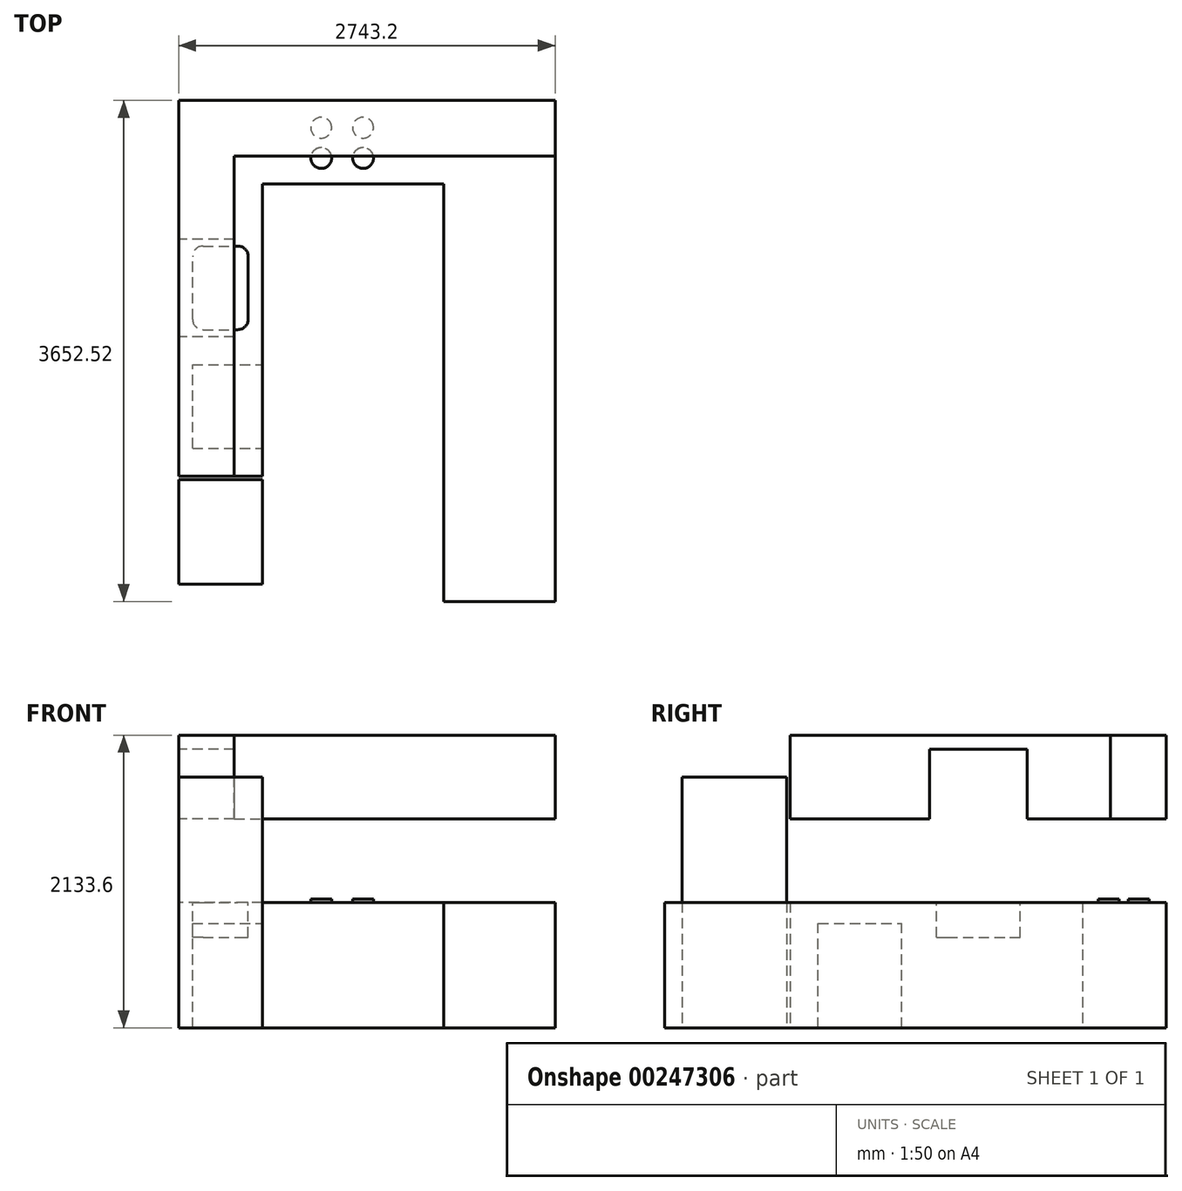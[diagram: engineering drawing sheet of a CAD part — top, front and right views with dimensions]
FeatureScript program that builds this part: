
annotation { "Feature Type Name" : "Feature", "Feature Type Description" : "" }
export const myFeature = defineFeature(function(context is Context, id is Id, definition is map)
    precondition{}
    {
        {
            var Q0;
            Q0=qCreatedBy(makeId("Top.planeOp"),FACE);
            var sketch = newSketch(context, id + "F0", { "sketchPlane" : qUnion([Q0])});
            skLineSegment(sketch, "E0.bottom", {"start": v(1371.6, -1826.26) * mm, "end": v(558.8, -1826.26) * mm});
            skLineSegment(sketch, "E0.top", {"start": v(1371.6, 1826.26) * mm, "end": v(-1371.6, 1826.26) * mm});
            skLineSegment(sketch, "E0.left", {"start": v(1371.6, -1826.26) * mm, "end": v(1371.6, 1826.26) * mm});
            skLineSegment(sketch, "E0.right", {"start": v(-1371.6, -911.86) * mm, "end": v(-1371.6, 1826.26) * mm});
            skPoint(sketch, "E0.middle", {"position": v(0, 0) * mm});
            skLineSegment(sketch, "E1.0", {"start": v(-762, -911.86) * mm, "end": v(-762, 1216.66) * mm});
            skLineSegment(sketch, "E2.0", {"start": v(558.8, 1216.66) * mm, "end": v(-762, 1216.66) * mm});
            skLineSegment(sketch, "E3.0", {"start": v(558.8, -1826.26) * mm, "end": v(558.8, 1216.66) * mm});
            skLineSegment(sketch, "E4.0", {"start": v(-762, -911.86) * mm, "end": v(-1371.6, -911.86) * mm});
            skPoint(sketch, "E5.orphan", {"position": v(-1371.6, -1826.26) * mm});
            skSolve(sketch);
        }
        {
            var Q0;
            Q0 = qSketchRegion(id + "F0", true);
            extrude(context, id + "F1", {"entities" : qUnion([Q0]), "depth" : 914.4 * mm});
        }
        {
            var Q0;
            Q0=qCreatedBy(makeId("Top.planeOp"),FACE);
            var sketch = newSketch(context, id + "F2", { "sketchPlane" : qUnion([Q0])});
            skLineSegment(sketch, "E6.top", {"start": v(-1371.6, -1699.26) * mm, "end": v(-762, -1699.26) * mm});
            skLineSegment(sketch, "E6.left", {"start": v(-1371.6, -937.26) * mm, "end": v(-1371.6, -1699.26) * mm});
            skLineSegment(sketch, "E6.right", {"start": v(-762, -937.26) * mm, "end": v(-762, -1699.26) * mm});
            skLineSegment(sketch, "E7", {"start": v(-1371.6, -937.26) * mm, "end": v(-762, -937.26) * mm});
            skSolve(sketch);
        }
        {
            var Q0;
            Q0 = qSketchRegion(id + "F2", true);
            extrude(context, id + "F3", {"entities" : qUnion([Q0]), "operationType" : NewBodyOperationType.ADD, "depth" : 1828.8 * mm});
        }
        {
            var Q0;
            Q0=makeQuery(id+"F1.opExtrude","SWEPT_FACE",FACE,{"disambiguationData":[OSD([sQuery(id+"F0.wireOp",EDGE,"E1.0")])]});
            var sketch = newSketch(context, id + "F4", { "sketchPlane" : qUnion([Q0])});
            skLineSegment(sketch, "E8.bottom", {"start": v(-708.66, 0) * mm, "end": v(-99.06, 0) * mm});
            skLineSegment(sketch, "E8.top", {"start": v(-708.66, 762) * mm, "end": v(-99.06, 762) * mm});
            skLineSegment(sketch, "E8.left", {"start": v(-708.66, 0) * mm, "end": v(-708.66, 762) * mm});
            skLineSegment(sketch, "E8.right", {"start": v(-99.06, 0) * mm, "end": v(-99.06, 762) * mm});
            skSolve(sketch);
        }
        {
            var Q0;
            Q0 = qSketchRegion(id + "F4", true);
            extrude(context, id + "F5", {"entities" : qUnion([Q0]), "operationType" : NewBodyOperationType.REMOVE, "oppositeDirection" : true, "depth" : 508 * mm});
        }
        {
            var Q0;
            Q0=makeQuery(id+"F1.opExtrude","CAP_FACE",FACE,{"disambiguationData":[OSD([sQuery(id+"F0.wireOp",EDGE,"E0.bottom"),sQuery(id+"F0.wireOp",EDGE,"E0.top"),sQuery(id+"F0.wireOp",EDGE,"E0.left"),sQuery(id+"F0.wireOp",EDGE,"E0.right"),sQuery(id+"F0.wireOp",EDGE,"E1.0"),sQuery(id+"F0.wireOp",EDGE,"E2.0"),sQuery(id+"F0.wireOp",EDGE,"E3.0"),sQuery(id+"F0.wireOp",EDGE,"E4.0")])],"isStart":false});
            var sketch = newSketch(context, id + "F6", { "sketchPlane" : qUnion([Q0])});
            skLineSegment(sketch, "E9.bottom", {"start": v(-1193.8, 154.94) * mm, "end": v(-939.8, 154.94) * mm});
            skLineSegment(sketch, "E9.top", {"start": v(-1193.8, 764.54) * mm, "end": v(-939.8, 764.54) * mm});
            skLineSegment(sketch, "E9.left", {"start": v(-1270, 231.14) * mm, "end": v(-1270, 688.34) * mm});
            skLineSegment(sketch, "E9.right", {"start": v(-863.6, 231.14) * mm, "end": v(-863.6, 688.34) * mm});
            skPoint(sketch, "E10.visualSharp", {"position": v(-1270, 154.94) * mm});
            skArc(sketch, "E10.filletArc", {"start": v(-1270, 231.14) * mm, "mid": v(-1247.68, 177.26) * mm, "end": v(-1193.8, 154.94) * mm});
            skPoint(sketch, "E11.visualSharp", {"position": v(-863.6, 154.94) * mm});
            skArc(sketch, "E11.filletArc", {"start": v(-939.8, 154.94) * mm, "mid": v(-885.92, 177.26) * mm, "end": v(-863.6, 231.14) * mm});
            skPoint(sketch, "E12.visualSharp", {"position": v(-863.6, 764.54) * mm});
            skArc(sketch, "E12.filletArc", {"start": v(-863.6, 688.34) * mm, "mid": v(-885.92, 742.22) * mm, "end": v(-939.8, 764.54) * mm});
            skPoint(sketch, "E13.visualSharp", {"position": v(-1270, 764.54) * mm});
            skArc(sketch, "E13.filletArc", {"start": v(-1193.8, 764.54) * mm, "mid": v(-1247.68, 742.22) * mm, "end": v(-1270, 688.34) * mm});
            skSolve(sketch);
        }
        {
            var Q0;
            Q0 = qSketchRegion(id + "F6", true);
            extrude(context, id + "F7", {"entities" : qUnion([Q0]), "operationType" : NewBodyOperationType.REMOVE, "oppositeDirection" : true, "depth" : 254 * mm});
        }
        {
            var Q0;
            Q0=makeQuery(id+"F1.opExtrude","CAP_FACE",FACE,{"disambiguationData":[OSD([sQuery(id+"F0.wireOp",EDGE,"E0.bottom"),sQuery(id+"F0.wireOp",EDGE,"E0.top"),sQuery(id+"F0.wireOp",EDGE,"E0.left"),sQuery(id+"F0.wireOp",EDGE,"E0.right"),sQuery(id+"F0.wireOp",EDGE,"E1.0"),sQuery(id+"F0.wireOp",EDGE,"E2.0"),sQuery(id+"F0.wireOp",EDGE,"E3.0"),sQuery(id+"F0.wireOp",EDGE,"E4.0")])],"isStart":false});
            var sketch = newSketch(context, id + "F8", { "sketchPlane" : qUnion([Q0])});
            skCircle(sketch, "E14", {"center": v(-331.95, 1406.1) * mm, "radius": 76.2 * mm});
            skCircle(sketch, "E15", {"center": v(-331.95, 1627.46) * mm, "radius": 76.2 * mm});
            skCircle(sketch, "E16", {"center": v(-27.15, 1406.1) * mm, "radius": 76.2 * mm});
            skCircle(sketch, "E17", {"center": v(-27.15, 1627.46) * mm, "radius": 76.2 * mm});
            skSolve(sketch);
        }
        {
            var Q0;
            Q0 = qSketchRegion(id + "F8", true);
            extrude(context, id + "F9", {"entities" : qUnion([Q0]), "operationType" : NewBodyOperationType.ADD, "depth" : 25.4 * mm});
        }
        {
            var Q0;
            Q0=makeQuery(id+"F1.opExtrude","SWEPT_FACE",FACE,{"disambiguationData":[OSD([sQuery(id+"F0.wireOp",EDGE,"E0.right")])]});
            var sketch = newSketch(context, id + "F10", { "sketchPlane" : qUnion([Q0])});
            skLineSegment(sketch, "E18.bottom", {"start": v(-1826.26, 2133.6) * mm, "end": v(911.86, 2133.6) * mm});
            skLineSegment(sketch, "E18.top", {"start": v(-104.14, 1524) * mm, "end": v(911.86, 1524) * mm});
            skLineSegment(sketch, "E18.left", {"start": v(911.86, 2133.6) * mm, "end": v(911.86, 1524) * mm});
            skLineSegment(sketch, "E18.right", {"start": v(-1826.26, 2133.6) * mm, "end": v(-1826.26, 1524) * mm});
            skLineSegment(sketch, "E19.top", {"start": v(-815.34, 2032) * mm, "end": v(-104.14, 2032) * mm});
            skLineSegment(sketch, "E19.left", {"start": v(-815.34, 1524) * mm, "end": v(-815.34, 2032) * mm});
            skLineSegment(sketch, "E19.right", {"start": v(-104.14, 1524) * mm, "end": v(-104.14, 2032) * mm});
            skLineSegment(sketch, "E20.trimOffspring", {"start": v(-1826.26, 1524) * mm, "end": v(-815.34, 1524) * mm});
            skSolve(sketch);
        }
        {
            var Q0;
            Q0 = qSketchRegion(id + "F10", true);
            extrude(context, id + "F11", {"entities" : qUnion([Q0]), "oppositeDirection" : true, "depth" : 406.4 * mm});
        }
        {
            var Q0;
            Q0=makeQuery(id+"F1.opExtrude","SWEPT_FACE",FACE,{"disambiguationData":[OSD([sQuery(id+"F0.wireOp",EDGE,"E0.top")])]});
            var sketch = newSketch(context, id + "F12", { "sketchPlane" : qUnion([Q0])});
            skLineSegment(sketch, "E21.bottom", {"start": v(965.2, 2133.6) * mm, "end": v(-1371.6, 2133.6) * mm});
            skLineSegment(sketch, "E21.top", {"start": v(965.2, 1524) * mm, "end": v(-1371.6, 1524) * mm});
            skLineSegment(sketch, "E21.left", {"start": v(965.2, 2133.6) * mm, "end": v(965.2, 1524) * mm});
            skLineSegment(sketch, "E21.right", {"start": v(-1371.6, 2133.6) * mm, "end": v(-1371.6, 1524) * mm});
            skSolve(sketch);
        }
        {
            var Q0;
            Q0 = qSketchRegion(id + "F12", true);
            extrude(context, id + "F13", {"entities" : qUnion([Q0]), "operationType" : NewBodyOperationType.ADD, "oppositeDirection" : true, "depth" : 406.4 * mm});
        }
    });
